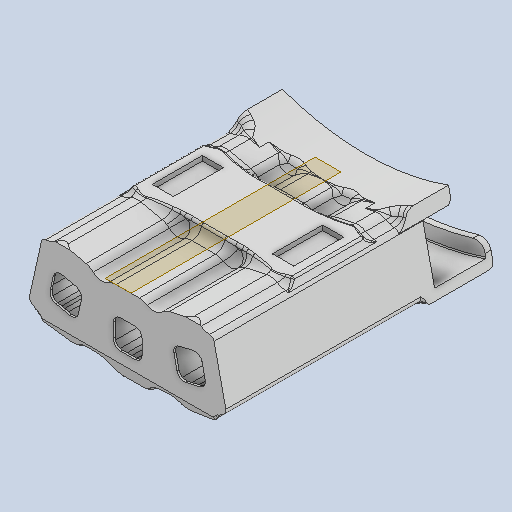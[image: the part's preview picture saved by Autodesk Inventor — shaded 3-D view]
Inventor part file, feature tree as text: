
AUTODESK INVENTOR PART (.ipt)
format: ipt  version: 2022 (Build 260153000, 153)  size: 2,612,736 bytes
history: native  units: mm
features: reference x32, projected_geometry x27, extrude x20, fillet x20, sketch x19, other x11, chamfer x1, mirror x1
ambient origin geometry x8: Origin, YZ Plane, XZ Plane, XY Plane, X Axis, Y Axis, Z Axis, Center Point
bodies: Body1 (feature_tree)
feature tree (131):
  other  "Твердое тело1"
  extrude  "Выдавливание1"  Depth=1.0mm
  extrude  "Выдавливание2"  Depth=1.0mm
  fillet  "Сопряжение5"  Radius=1.0mm
  fillet  "Сопряжение6"  Radius=1.0mm
  extrude  "Выдавливание6"  Depth=43.0mm TaperAngle=0.0deg
  sketch  "Эскиз8"
  sketch  "Эскиз9"
  extrude  "Выдавливание7"  Depth=0.4mm TaperAngle=0.0deg
  extrude  "Выдавливание8"  Depth=1.0mm
  extrude  "Выдавливание9"  Depth=6.0mm
  extrude  "Выдавливание10"  Depth=6.0mm
  fillet  "Сопряжение7"  Radius=6.0mm
  fillet  "Сопряжение8"  Radius=6.0mm
  fillet  "Сопряжение9"  Radius=6.0mm
  fillet  "Сопряжение10"  Radius=6.0mm
  extrude  "Выдавливание11"  Depth=1.5mm
  extrude  "Выдавливание12"  Depth=5.0mm
  extrude  "Выдавливание13"  Depth=49.0mm TaperAngle=0.0deg
  fillet  "Сопряжение11"  Radius=5.0mm
  fillet  "Сопряжение12"  Radius=5.0mm
  fillet  "Сопряжение13"  Radius=49.0mm
  fillet  "Сопряжение15"  Radius=49.0mm
  fillet  "Сопряжение16"  Radius=2.0mm
  chamfer  "Фаска1"  Distance=2.0mm
  fillet  "Сопряжение28"  Radius=2.0mm
  fillet  "Сопряжение32"  Radius=2.0mm
  extrude  "Выдавливание27"  Depth=2.0mm
  extrude  "Выдавливание28"  Depth=2.0mm
  extrude  "Выдавливание29"  Depth=1.0mm
  fillet  "Сопряжение35"  Radius=1.0mm
  other  "РабПлоскость3"
  extrude  "Выдавливание30"  Depth=1.0mm
  extrude  "Выдавливание31"  Depth=1.0mm
  extrude  "Выдавливание32"  Depth=1.0mm
  extrude  "Выдавливание33"  Depth=1.0mm
  fillet  "Сопряжение36"  Radius=49.0mm
  fillet  "Сопряжение37"  Radius=43.0mm
  fillet  "Сопряжение38"  Radius=4.0mm
  extrude  "Выдавливание34"  Depth=2.5mm
  fillet  "Сопряжение39"  Radius=3.0mm
  fillet  "Сопряжение40"  Radius=0.5mm
  extrude  "Выдавливание35"  Depth=2.0mm
  extrude  "Выдавливание36"  Depth=10.7mm TaperAngle=0.0deg
  mirror  "Зеркальное отражение1"
  fillet  "Сопряжение42"  Radius=3.0mm
  sketch  "Эскиз1"
  reference  "Ссылка1"
  reference  "Ссылка2"
  reference  "Ссылка3"
  reference  "Ссылка4"
  reference  "Ссылка5"
  reference  "Ссылка6"
  reference  "Ссылка7"
  reference  "Ссылка8"
  reference  "Ссылка9"
  reference  "Ссылка10"
  reference  "Ссылка11"
  reference  "Ссылка12"
  reference  "Ссылка13"
  sketch  "Эскиз2"
  projected_geometry  "Спроецированная петля1"
  sketch  "Эскиз7"
  projected_geometry  "Спроецированная петля4"
  projected_geometry  "Спроецированная петля5"
  projected_geometry  "Спроецированная петля6"
  projected_geometry  "Спроецированная петля7"
  sketch  "Эскиз10"
  projected_geometry  "Спроецированная петля8"
  projected_geometry  "Спроецированная петля9"
  projected_geometry  "Спроецированная петля10"
  projected_geometry  "Спроецированная петля11"
  sketch  "Эскиз11"
  projected_geometry  "Спроецированная петля12"
  sketch  "Эскиз12"
  projected_geometry  "Спроецированная петля13"
  projected_geometry  "Спроецированная петля14"
  reference  "Ссылка14"
  reference  "Ссылка15"
  reference  "Ссылка16"
  reference  "Ссылка17"
  reference  "Ссылка18"
  reference  "Ссылка19"
  reference  "Ссылка20"
  reference  "Ссылка21"
  reference  "Ссылка22"
  reference  "Ссылка23"
  reference  "Ссылка24"
  reference  "Ссылка25"
  reference  "Ссылка26"
  sketch  "Эскиз13"
  projected_geometry  "Спроецированная петля15"
  sketch  "Эскиз14"
  projected_geometry  "Спроецированная петля16"
  reference  "Ссылка27"
  reference  "Ссылка28"
  sketch  "Эскиз30"
  reference  "Ссылка31"
  projected_geometry  "Спроецированная петля50"
  reference  "Ссылка32"
  sketch  "Эскиз31"
  projected_geometry  "Спроецированная петля51"
  sketch  "Эскиз32"
  projected_geometry  "Спроецированная петля52"
  projected_geometry  "Спроецированная петля56"
  projected_geometry  "Спроецированная петля57"
  projected_geometry  "Спроецированная петля58"
  sketch  "Эскиз36"
  projected_geometry  "Спроецированная петля59"
  sketch  "Эскиз37"
  projected_geometry  "Спроецированная петля60"
  projected_geometry  "Спроецированная петля61"
  sketch  "Эскиз38"
  projected_geometry  "Спроецированная петля62"
  sketch  "Эскиз39"
  reference  "Ссылка33"
  sketch  "Эскиз40"
  projected_geometry  "Спроецированная петля63"
  projected_geometry  "Спроецированная петля64"
  reference  "Ссылка34"
  sketch  "Эскиз41"
  projected_geometry  "Спроецированная петля65"
  other  "<userpath>\Documents\Git\MZCAT_2024\MZCAT_2.iam"
  other  "MZCAT_2.iam"
  other  "vydacha_chertezh:1"
  other  "CAT_protector:1"
  other  "<userpath>\Documents\Git\MZCAT_2024\MZCAT_4.iam"
  other  "MZCAT_4.iam"
  other  "magazine_fixator:1"
  other  "<userpath>\Documents\Git\MZCAT_2024\MZCAT_4.iam"
  other  "vydacha_pusher:1"
